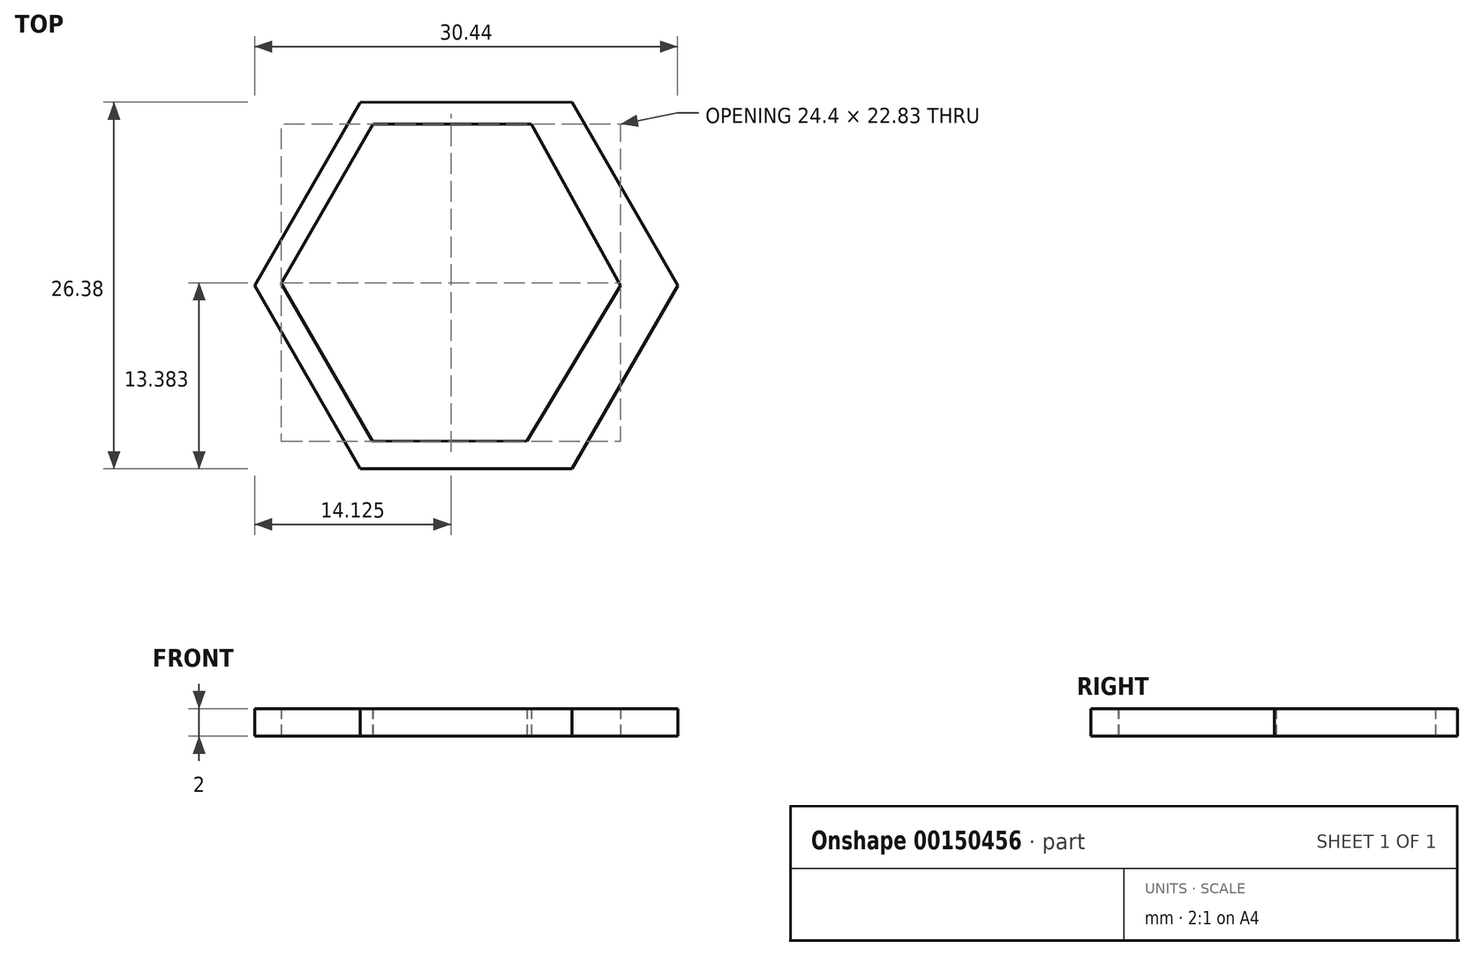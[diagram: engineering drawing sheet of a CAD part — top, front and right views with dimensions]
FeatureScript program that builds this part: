
annotation { "Feature Type Name" : "Feature", "Feature Type Description" : "" }
export const myFeature = defineFeature(function(context is Context, id is Id, definition is map)
    precondition{}
    {
        {
            var Q0;
            Q0=qCreatedBy(makeId("Top.planeOp"),FACE);
            var sketch = newSketch(context, id + "F0", { "sketchPlane" : qUnion([Q0])});
            skLineSegment(sketch, "E0.0", {"start": v(-7.6, -13.19) * mm, "end": v(-15.22, 0) * mm});
            skLineSegment(sketch, "E0.1", {"start": v(-15.22, 0) * mm, "end": v(-7.62, 13.18) * mm});
            skLineSegment(sketch, "E0.2", {"start": v(-7.62, 13.18) * mm, "end": v(7.6, 13.19) * mm});
            skLineSegment(sketch, "E0.3", {"start": v(7.6, 13.19) * mm, "end": v(15.22, 0) * mm});
            skLineSegment(sketch, "E0.4", {"start": v(15.22, 0) * mm, "end": v(7.62, -13.18) * mm});
            skLineSegment(sketch, "E0.5", {"start": v(7.62, -13.18) * mm, "end": v(-7.6, -13.19) * mm});
            skPoint(sketch, "E1.cCircle.center.orphan", {"position": v(0, -0.12) * mm});
            skLineSegment(sketch, "E2.0", {"start": v(-6.73, -11.22) * mm, "end": v(-13.3, 0.14) * mm});
            skLineSegment(sketch, "E2.1", {"start": v(-13.3, 0.14) * mm, "end": v(-6.69, 11.6) * mm});
            skLineSegment(sketch, "E2.2", {"start": v(-6.69, 11.6) * mm, "end": v(4.68, 11.6) * mm});
            skLineSegment(sketch, "E2.3", {"start": v(4.68, 11.6) * mm, "end": v(11.1, 0) * mm});
            skLineSegment(sketch, "E2.4", {"start": v(11.1, 0) * mm, "end": v(4.38, -11.2) * mm});
            skLineSegment(sketch, "E2.5", {"start": v(4.38, -11.2) * mm, "end": v(-6.73, -11.22) * mm});
            skSolve(sketch);
        }
        {
            var Q0;
            Q0 = qSketchRegion(id + "F0", true);
            var Q1;
            Q1=makeQuery(id+"F0.imprint","IMPRINT",FACE,{"disambiguationData":[TD([[makeQuery(id+"F0.imprint","IMPRINT",EDGE,{"derivedFrom":sQuery(id+"F0.wireOp",EDGE,"E0.0")}),-1.0]])]});
            extrude(context, id + "F1", {"entities" : qUnion([Q0, Q1]), "depth" : 2 * mm});
        }
    });
